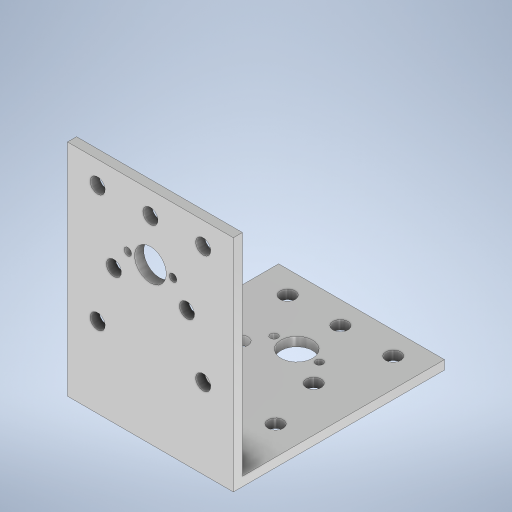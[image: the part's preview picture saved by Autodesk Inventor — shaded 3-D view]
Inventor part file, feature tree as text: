
AUTODESK INVENTOR PART (.ipt)
format: ipt  version: 2024 (Build 280153000, 153)  size: 298,496 bytes
history: native  units: in
note: dims shown in document units (in); Inventor stores cm internally (conversion verified against a paired STEP export)
features: sketch x8, hole x6, extrude x2, other x2, plane x1
ambient origin geometry x8: Origin, YZ Plane, XZ Plane, XY Plane, X Axis, Y Axis, Z Axis, Center Point
bodies: Solid1 (feature_tree)
feature tree (19):
  plane  "Work Plane1"
  extrude  "Extrusion1"  Depth=0.3937in
  extrude  "Extrusion2"  Depth=0.5512in
  hole  "Hole1"  [1 undecoded]
  hole  "Hole2"  [1 undecoded]
  hole  "Hole3"  [1 undecoded]
  sketch  "Sketch1"  dims[d5=2.7559in d6=0.0in]
  sketch  "Sketch2"  dims[d7=0.4134in d8=0.2953in d9=0.1476in d10=0.0984in d11=90.0deg d12=0.3937in d13=0.8108in]
  sketch  "Sketch3"  dims[d16=0.0984in d17=0.2953in d18=0.1476in d19=0.0984in d20=90.0deg d21=0.3937in d22=0.8108in]
  sketch  "Sketch4"  dims[d31=0.1969in d32=0.2953in d33=0.1476in d34=0.0984in d35=90.0deg d36=0.3937in d37=0.8108in d40=0.8465in]
  sketch  "Sketch5"  dims[d41=1.0827in d42=0.5512in]
  sketch  "Sketch6"  dims[d43=0.689in d44=0.689in]
  sketch  "Sketch7"  dims[d45=1.5354in d46=0.2953in]
  sketch  "Sketch8"  dims[d47=0.2953in d48=0.2953in d51=0.8108in d52=90.0deg d53=0.0984in d54=0.1476in d55=0.3937in d56=0.4134in d57=0.2953in d58=0.2953in d59=0.2953in d60=0.8108in d61=90.0deg d62=0.0984in d63=0.1476in d64=0.3937in d65=0.0984in d66=0.2953in d71=0.8108in d72=90.0deg d73=0.0984in d74=0.1476in d75=0.3937in d76=0.1969in d77=0.8465in d78=1.0827in d79=0.689in d80=0.689in d81=0.5512in d82=1.5354in]
  other  "Assembly1"
  other  "Base_Aluminum Plate:1"
  hole  "Hole6"  [1 undecoded]
  hole  "Hole4"  [1 undecoded]
  hole  "Hole5"  [1 undecoded]
note: 6 required parameter values undecoded (feature->parameter linkage not recoverable at this tier; creation-order binding heuristic only, values carry confidence <= 0.55)
